# Revit family: РИДАН_BVR-FR_Кран шаровой ГОСТ полнопроходной с накидной гайкой и ниппелем
name_source: partatom
category: Арматура трубопроводов
units: mm (PartAtom-declared; Revit-internal decimal feet)

## family parameters
Всегда вертикально = Да
На основе рабочей плоскости = Нет
Общий = Нет
При загрузке вырезать с полостями = Нет
Размер круглого соединителя = Использовать диаметр
Тип детали = Вставляется

## types (4) — shared parameters
ADSK_Версия Revit = 2019
ADSK_Версия семейства = 1.0
ADSK_Единица измерения = шт.
ADSK_Завод-изготовитель = ООО «Ридан-Трейд»
ADSK_Количество = 1
LT = BVR-FR
URL = https://ridan.ru
t = 1.25 мм
z = 17 мм
Корпус = Латунь никелированная
Ручка_цвет = Ручка

## per-type parameters (varying)
- DN15: ADSK_Диаметр условный=15 мм; ADSK_Код изделия=065B8303RG; ADSK_Марка=BVR-FR DN15; ADSK_Масса=0.27; ADSK_Наименование=Кран шаровой ГОСТ BVR-FR полнопроходной с накидной гайкой и ниппелем PN40, Tmax=120C, DN15; a=17 мм; a1=11.5 мм; b=30 мм; b1=3.62 мм; c=27.5 мм; c1=2 мм; d=26.4 мм; d1=4 мм; e=23.5 мм; e1=6.25 мм; f=20.7 мм; f1=5.62 мм; g=18.3 мм; g1=20.91 мм; h=20 мм; h1=11.5 мм; i=25 мм; i1=3 мм; j=27.5 мм; j1=4 мм; k=30 мм; k1=16.5 мм; l=1.2 мм; l1=5 мм; m=17.3 мм; m1=12.5 мм; n=12 мм; n1=8.63 мм; o=0.8 мм; o1=13 мм; p=0.78 мм; p1=4 мм; q=2.5 мм; r=1.15 мм; r1=19 мм; s=12.85 мм; s1=9.85 мм; t1=52.23 мм; u=12.25 мм; v=1.08 мм; w=8.92 мм; x=15 мм; y=10.35 мм; Длина_УГО=52.23 мм
- DN20: ADSK_Диаметр условный=20 мм; ADSK_Код изделия=065B8304RG; ADSK_Марка=BVR-FR DN20; ADSK_Масса=0.37; ADSK_Наименование=Кран шаровой ГОСТ BVR-FR полнопроходной с накидной гайкой и ниппелем PN40, Tmax=120C, DN20; a=19.5 мм; a1=8.88 мм; b=36.5 мм; b1=3.62 мм; c=33 мм; c1=2 мм; d=31.81 мм; d1=4 мм; e=29.5 мм; e1=6.13 мм; f=26.4 мм; f1=5.74 мм; g=24 мм; g1=20.91 мм; h=25 мм; h1=11.5 мм; i=30 мм; i1=3 мм; j=33 мм; j1=4 мм; k=35.5 мм; k1=16.5 мм; l=1.2 мм; l1=5 мм; m=19.8 мм; m1=12.5 мм; n=13 мм; n1=8.63 мм; o=0.8 мм; o1=13 мм; p=0.62 мм; p1=4 мм; q=1.25 мм; r=1.01 мм; r1=24.5 мм; s=14.99 мм; s1=11.1 мм; t1=54.57 мм; u=11.75 мм; v=0.47 мм; w=10.03 мм; x=15 мм; y=9.99 мм; Длина_УГО=54.57 мм
- DN25: ADSK_Диаметр условный=25 мм; ADSK_Код изделия=065B8305RG; ADSK_Марка=BVR-FR DN25; ADSK_Масса=0.63; ADSK_Наименование=Кран шаровой ГОСТ BVR-FR полнопроходной с накидной гайкой и ниппелем PN40, Tmax=120C, DN25; a=28 мм; a1=10.74 мм; b=47 мм; b1=4.76 мм; c=41.9 мм; c1=5 мм; d=41.5 мм; d1=5.81 мм; e=37 мм; e1=9.19 мм; f=33 мм; f1=7.07 мм; g=30 мм; g1=26.05 мм; h=35 мм; h1=12.5 мм; i=37 мм; i1=4 мм; j=41.5 мм; j1=6 мм; k=44 мм; k1=18 мм; l=1.5 мм; l1=5 мм; m=21.5 мм; m1=15.5 мм; n=14 мм; n1=9.39 мм; o=0.8 мм; o1=17 мм; p=1.29 мм; p1=5.97 мм; q=3.5 мм; r=1.3 мм; r1=30.5 мм; s=16.7 мм; s1=12.25 мм; t1=62.84 мм; u=13.25 мм; v=0.6 мм; w=13.4 мм; x=19 мм; y=11.7 мм; Длина_УГО=62.84 мм
- DN32: ADSK_Диаметр условный=32 мм; ADSK_Код изделия=065B8306RG; ADSK_Марка=BVR-FR DN32; ADSK_Масса=0.9; ADSK_Наименование=Кран шаровой ГОСТ BVR-FR полнопроходной с накидной гайкой и ниппелем PN40, Tmax=120C, DN32; a=34 мм; a1=13.05 мм; b=53 мм; b1=5.76 мм; c=53 мм; c1=1.19 мм; d=47.8 мм; d1=2.18 мм; e=46.13 мм; e1=4.14 мм; f=41.9 мм; f1=20.45 мм; g=38.11 мм; g1=31.01 мм; h=45 мм; h1=15.17 мм; i=47 мм; i1=4.85 мм; j=54.5 мм; j1=7.28 мм; k=57 мм; k1=21.84 мм; l=1.5 мм; l1=6.07 мм; m=28.5 мм; m1=18.81 мм; n=16 мм; n1=11.4 мм; o=3.72 мм; o1=17 мм; p=0.48 мм; p1=7.5 мм; q=4.71 мм; r=4.19 мм; r1=39 мм; s=24.5 мм; s1=15.75 мм; t1=83.85 мм; u=14.75 мм; v=0.94 мм; w=15.56 мм; x=22 мм; y=15.13 мм; Длина_УГО=83.85 мм
